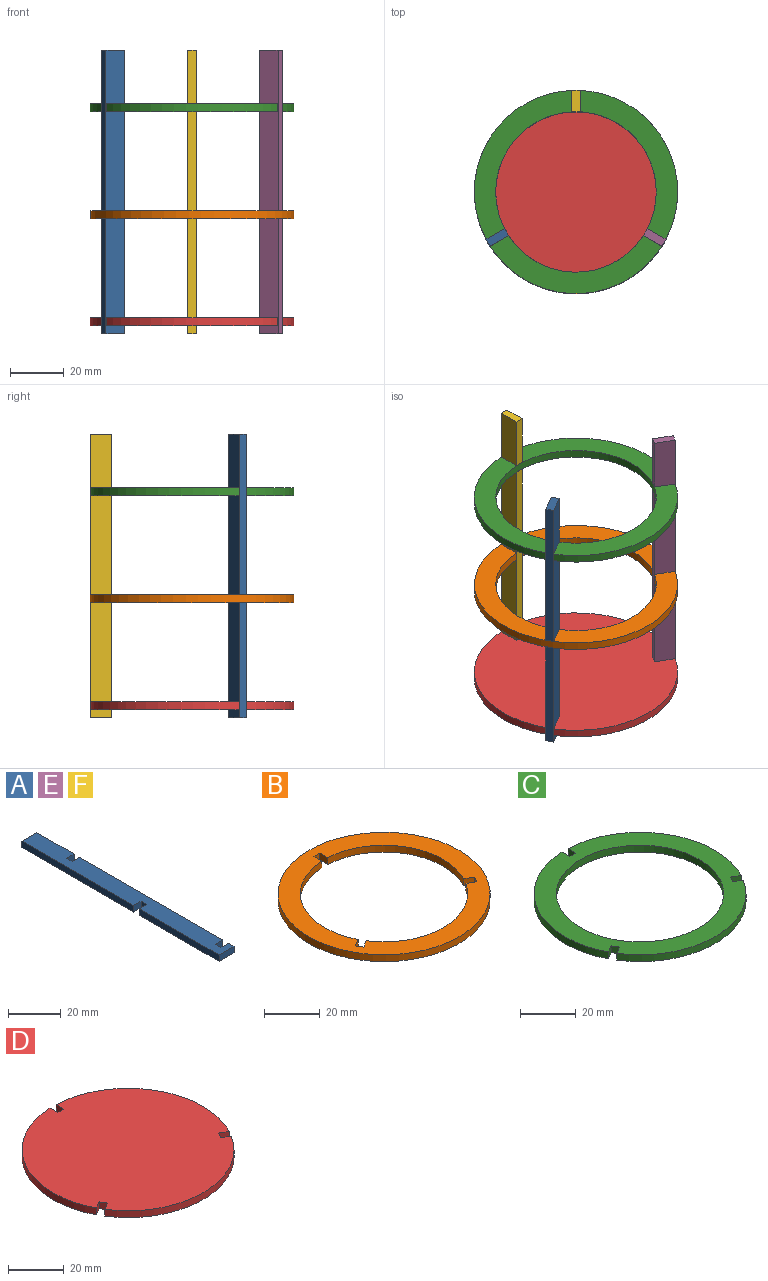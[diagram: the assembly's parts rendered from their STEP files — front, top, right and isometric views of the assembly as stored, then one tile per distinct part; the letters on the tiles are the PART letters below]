
ASSEMBLY  parts=6 mates=15
PART A: 18 faces, bbox 8x106x3 mm
  f0: plane 8x3mm, normal (0,-1,0), area 24mm2, adj f1,f15,f16,f17
  f1: plane 3x3mm, normal (1,0,0), area 9mm2, adj f0,f2,f16,f17
  f2: plane 4x3mm, normal (0,1,0), area 12mm2, adj f1,f3,f16,f17
  f3: plane 3x3mm, normal (1,0,0), area 9mm2, adj f2,f4,f16,f17
  f4: plane 4x3mm, normal (0,-1,0), area 12mm2, adj f3,f5,f16,f17
  f5: plane 77x3mm, normal (1,0,0), area 231mm2, adj f4,f6,f16,f17
  f6: plane 4x3mm, normal (0,1,0), area 12mm2, adj f5,f7,f16,f17
  f7: plane 3x3mm, normal (1,0,0), area 9mm2, adj f6,f8,f16,f17
  f8: plane 4x3mm, normal (0,-1,0), area 12mm2, adj f7,f9,f16,f17
  f9: plane 20x3mm, normal (1,0,0), area 60mm2, adj f8,f10,f16,f17
  f10: plane 8x3mm, normal (0,1,0), area 24mm2, adj f9,f11,f16,f17
  f11: plane 60x3mm, normal (-1,0,0), area 180mm2, adj f10,f12,f16,f17
  f12: plane 4x3mm, normal (0,-1,0), area 12mm2, adj f11,f13,f16,f17
  f13: plane 3x3mm, normal (-1,0,0), area 9mm2, adj f12,f14,f16,f17
  f14: plane 4x3mm, normal (0,1,0), area 12mm2, adj f13,f15,f16,f17
  f15: plane 43x3mm, normal (-1,0,0), area 129mm2, adj f0,f14,f16,f17
  f16: plane 106x8mm, normal (0,0,1), area 812mm2, adj f0,f1,f2,f3,f4,f5,f6,f7
  f17: plane 106x8mm, normal (0,0,-1), area 812mm2, adj f0,f1,f2,f3,f4,f5,f6,f7
PART B: 15 faces, bbox 76x76x3 mm
  f0: plane 3x2.6mm, normal (0.87,0.5,0), area 9mm2, adj f1,f12,f13,f14
  f1: plane 3.5x3mm, normal (0.5,-0.87,0), area 12.1mm2, adj f0,f2,f13,f14
  f2: cylinder r=30mm len=43.64mm, axis (0,0,-1), area 179.5mm2, adj f1,f3,f13,f14
  f3: plane 4.04x3mm, normal (1,0,0), area 12.1mm2, adj f2,f4,f13,f14
  f4: plane 3x3mm, normal (0,-1,0), area 9mm2, adj f3,f5,f13,f14
  f5: plane 4.04x3mm, normal (-1,0,0), area 12.1mm2, adj f4,f6,f13,f14
  f6: cylinder r=30mm len=43.64mm, axis (0,0,-1), area 179.5mm2, adj f5,f7,f13,f14
  f7: plane 3.5x3mm, normal (-0.5,-0.87,0), area 12.1mm2, adj f6,f8,f13,f14
  f8: plane 3x2.6mm, normal (-0.87,0.5,0), area 9mm2, adj f7,f9,f13,f14
  f9: plane 3.5x3mm, normal (0.5,0.87,0), area 12.1mm2, adj f8,f10,f13,f14
  f10: cylinder r=30mm len=50.4mm, axis (0,0,-1), area 179.5mm2, adj f9,f12,f13,f14
  f11: cylinder r=38mm len=76mm, axis (0,0,-1), area 716.3mm2, adj f13,f14
  f12: plane 3.5x3mm, normal (-0.5,0.87,0), area 12.1mm2, adj f0,f10,f13,f14
  f13: plane 76x76mm, normal (0,0,1), area 1672.9mm2, adj f0,f1,f2,f3,f4,f5,f6,f7
  f14: plane 76x76mm, normal (0,0,-1), area 1672.9mm2, adj f0,f1,f2,f3,f4,f5,f6,f7
PART C: 15 faces, bbox 76x76x3 mm
  f0: plane 3.97x3mm, normal (1,0,0), area 11.9mm2, adj f1,f11,f13,f14
  f1: cylinder r=38mm len=55.66mm, axis (0,0,-1), area 229.8mm2, adj f0,f2,f13,f14
  f2: plane 3.44x3mm, normal (0.5,-0.87,0), area 11.9mm2, adj f1,f3,f13,f14
  f3: plane 3x2.6mm, normal (-0.87,-0.5,0), area 9mm2, adj f2,f4,f13,f14
  f4: plane 3.44x3mm, normal (-0.5,0.87,0), area 11.9mm2, adj f3,f5,f13,f14
  f5: cylinder r=38mm len=64.27mm, axis (0,0,-1), area 229.8mm2, adj f4,f6,f13,f14
  f6: plane 3.44x3mm, normal (0.5,0.87,0), area 11.9mm2, adj f5,f7,f13,f14
  f7: plane 3x2.6mm, normal (0.87,-0.5,0), area 9mm2, adj f6,f8,f13,f14
  f8: plane 3.44x3mm, normal (-0.5,-0.87,0), area 11.9mm2, adj f7,f9,f13,f14
  f9: cylinder r=38mm len=55.66mm, axis (0,0,-1), area 229.8mm2, adj f8,f10,f13,f14
  f10: plane 3.97x3mm, normal (-1,0,0), area 11.9mm2, adj f9,f11,f13,f14
  f11: plane 3x3mm, normal (0,1,0), area 9mm2, adj f0,f10,f13,f14
  f12: cylinder r=30mm len=60mm, axis (0,0,-1), area 565.5mm2, adj f13,f14
  f13: plane 76x75.97mm, normal (0,0,1), area 1673.1mm2, adj f0,f1,f2,f3,f4,f5,f6,f7
  f14: plane 76x75.97mm, normal (0,0,-1), area 1673.1mm2, adj f0,f1,f2,f3,f4,f5,f6,f7
PART D: 14 faces, bbox 76x76x3 mm
  f0: plane 3.97x3mm, normal (1,0,0), area 11.9mm2, adj f1,f11,f12,f13
  f1: cylinder r=38mm len=55.66mm, axis (0,0,-1), area 229.8mm2, adj f0,f2,f12,f13
  f2: plane 3.44x3mm, normal (0.5,-0.87,0), area 11.9mm2, adj f1,f3,f12,f13
  f3: plane 3x2.6mm, normal (-0.87,-0.5,0), area 9mm2, adj f2,f4,f12,f13
  f4: plane 3.44x3mm, normal (-0.5,0.87,0), area 11.9mm2, adj f3,f5,f12,f13
  f5: cylinder r=38mm len=64.27mm, axis (0,0,-1), area 229.8mm2, adj f4,f6,f12,f13
  f6: plane 3.44x3mm, normal (0.5,0.87,0), area 11.9mm2, adj f5,f7,f12,f13
  f7: plane 3x2.6mm, normal (0.87,-0.5,0), area 9mm2, adj f6,f8,f12,f13
  f8: plane 3.44x3mm, normal (-0.5,-0.87,0), area 11.9mm2, adj f7,f9,f12,f13
  f9: cylinder r=38mm len=55.66mm, axis (0,0,-1), area 229.8mm2, adj f8,f10,f12,f13
  f10: plane 3.97x3mm, normal (-1,0,0), area 11.9mm2, adj f9,f11,f12,f13
  f11: plane 3x3mm, normal (0,1,0), area 9mm2, adj f0,f10,f12,f13
  f12: plane 76x75.97mm, normal (0,0,1), area 4500.5mm2, adj f0,f1,f2,f3,f4,f5,f6,f7
  f13: plane 76x75.97mm, normal (0,0,-1), area 4500.5mm2, adj f0,f1,f2,f3,f4,f5,f6,f7
PART E: same geometry as A
PART F: same geometry as A
PLACE A rot(axis=(0.94,0.25,0.25),93.8deg) t=(-30.19,-15.7,41.5)mm
PLACE B t=(0,0,40)mm
PLACE C t=(0,0,80)mm
PLACE D at identity
PLACE E rot(axis=(0.19,0.69,0.69),158.9deg) t=(28.69,-18.3,41.5)mm
PLACE F rot(axis=(0.58,-0.58,-0.58),120deg) t=(1.5,34,41.5)mm
MATE planar D.f7 <-> E.f3  axis (0.87,-0.5,0) through (29.44,-17,1.5)mm
MATE planar D.f11 <-> F.f3  axis (0,1,0) through (0,34,1.5)mm
MATE planar C.f2 <-> A.f17  axis (0.5,-0.87,0) through (-31.91,-16.69,81.5)mm
MATE planar C.f12 <-> E.f8  axis (0,0,1) through (0,0,83)mm
MATE planar F.f4 <-> D.f1  axis (0,0,-1) through (0,32,3)mm
MATE planar E.f4 <-> D.f1  axis (0,0,-1) through (27.71,-16,3)mm
MATE planar E.f17 <-> D.f6  axis (-0.5,-0.87,0) through (28.69,-18.3,40)mm
MATE cylindrical C.f12 <-> D.f1  axis (0,0,1) through (0,0,83)mm
MATE cylindrical B.f2 <-> D.f5  axis (0,0,1) through (0,0,43)mm
MATE planar A.f4 <-> D.f1  axis (0,0,-1) through (-27.71,-16,3)mm
MATE planar B.f9 <-> E.f17  axis (0.5,0.87,0) through (26.95,-17.29,41.5)mm
MATE planar B.f2 <-> E.f12  axis (0,0,1) through (0,0,43)mm
MATE planar F.f16 <-> D.f0  axis (-1,0,0) through (-1.5,34,41.5)mm
MATE planar A.f3 <-> D.f3  axis (0.87,0.5,0) through (-29.44,-17,1.5)mm
MATE planar A.f17 <-> D.f2  axis (-0.5,0.87,0) through (-30.19,-15.7,40)mm
